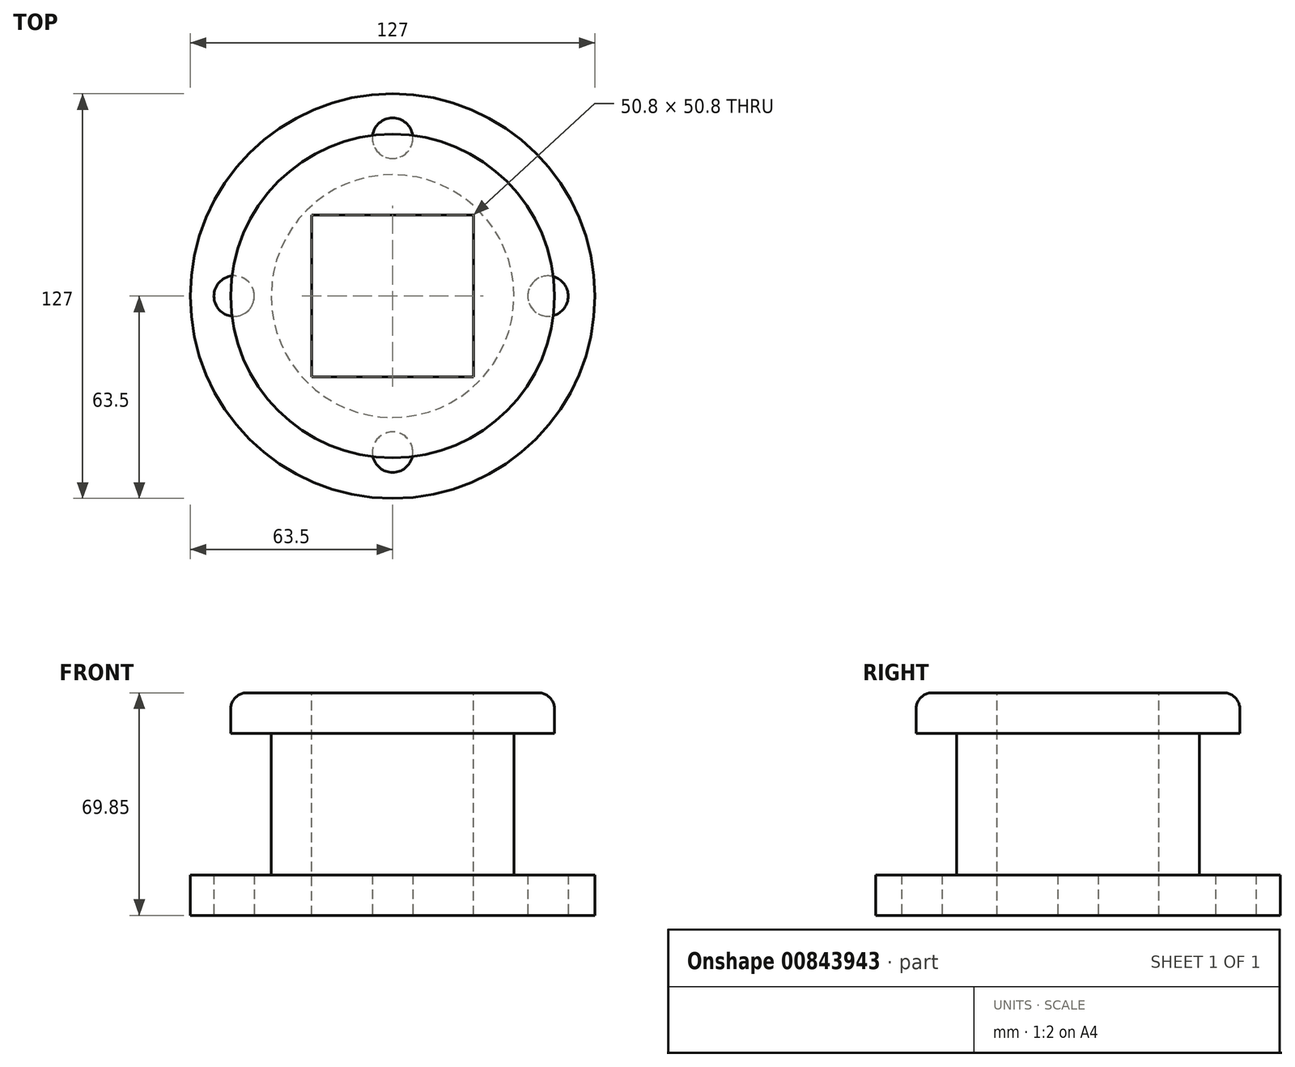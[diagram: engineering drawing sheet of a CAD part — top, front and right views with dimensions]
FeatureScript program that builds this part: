
annotation { "Feature Type Name" : "Feature", "Feature Type Description" : "" }
export const myFeature = defineFeature(function(context is Context, id is Id, definition is map)
    precondition{}
    {
        {
            var Q0;
            Q0=qCreatedBy(makeId("Top.planeOp"),FACE);
            var sketch = newSketch(context, id + "F0", { "sketchPlane" : qUnion([Q0])});
            skCircle(sketch, "E0", {"center": v(0, 0) * mm, "radius": 63.5 * mm});
            skSolve(sketch);
        }
        {
            var Q0;
            Q0 = qSketchRegion(id + "F0", true);
            extrude(context, id + "F1", {"entities" : qUnion([Q0]), "depth" : 12.7 * mm, "offsetDistance" : 25.4 * mm});
        }
        {
            var Q0;
            Q0=qCreatedBy(makeId("Top.planeOp"),FACE);
            var sketch = newSketch(context, id + "F2", { "sketchPlane" : qUnion([Q0])});
            skCircle(sketch, "E1", {"center": v(0, 0) * mm, "radius": 38.1 * mm});
            skSolve(sketch);
        }
        {
            var Q0;
            Q0 = qSketchRegion(id + "F2", true);
            extrude(context, id + "F3", {"entities" : qUnion([Q0]), "operationType" : NewBodyOperationType.ADD, "depth" : 57.15 * mm, "offsetDistance" : 25.4 * mm});
        }
        {
            var Q0;
            Q0=qCreatedBy(makeId("Top.planeOp"),FACE);
            var sketch = newSketch(context, id + "F4", { "sketchPlane" : qUnion([Q0])});
            skCircle(sketch, "E2", {"center": v(-49.74, 0) * mm, "radius": 6.35 * mm});
            skPoint(sketch, "E3.center.orphan", {"position": v(0, 49.55) * mm});
            skPoint(sketch, "E4.center.orphan", {"position": v(48.79, 0) * mm});
            skPoint(sketch, "E5.center.orphan", {"position": v(0, -48.98) * mm});
            skCircle(sketch, "E6", {"center": v(0, 49.55) * mm, "radius": 6.35 * mm});
            skCircle(sketch, "E7", {"center": v(48.79, 0) * mm, "radius": 6.35 * mm});
            skCircle(sketch, "E8", {"center": v(0, -48.98) * mm, "radius": 6.35 * mm});
            skSolve(sketch);
        }
        {
            var Q0;
            Q0 = qSketchRegion(id + "F4", true);
            extrude(context, id + "F5", {"entities" : qUnion([Q0]), "operationType" : NewBodyOperationType.REMOVE, "oppositeDirection" : true, "depth" : 12.7 * mm, "offsetDistance" : 25.4 * mm});
        }
        {
            var Q0;
            Q0 = qSketchRegion(id + "F4", true);
            extrude(context, id + "F6", {"entities" : qUnion([Q0]), "operationType" : NewBodyOperationType.REMOVE, "depth" : 25.4 * mm, "offsetDistance" : 25.4 * mm});
        }
        {
            var Q0;
            Q0 = qSketchRegion(id + "F4", true);
            extrude(context, id + "F7", {"entities" : qUnion([Q0]), "operationType" : NewBodyOperationType.REMOVE, "oppositeDirection" : true, "depth" : 25.4 * mm, "offsetDistance" : 25.4 * mm});
        }
        {
            var Q0;
            Q0=makeQuery(id+"F3.opExtrude","CAP_FACE",FACE,{"disambiguationData":[OSD([sQuery(id+"F2.wireOp",EDGE,"E1")])],"isStart":false});
            var sketch = newSketch(context, id + "F8", { "sketchPlane" : qUnion([Q0])});
            skCircle(sketch, "E9", {"center": v(0, 0) * mm, "radius": 50.8 * mm});
            skSolve(sketch);
        }
        {
            var Q0;
            Q0 = qSketchRegion(id + "F8", true);
            extrude(context, id + "F9", {"entities" : qUnion([Q0]), "operationType" : NewBodyOperationType.ADD, "depth" : 12.7 * mm, "offsetDistance" : 25.4 * mm});
        }
        {
            var Q0;
            Q0=makeQuery(id+"F9.opExtrude","CAP_FACE",FACE,{"disambiguationData":[OSD([sQuery(id+"F8.wireOp",EDGE,"E9")])],"isStart":false});
            var sketch = newSketch(context, id + "F10", { "sketchPlane" : qUnion([Q0])});
            skLineSegment(sketch, "E10.bottom", {"start": v(-25.4, 25.4) * mm, "end": v(25.4, 25.4) * mm});
            skLineSegment(sketch, "E10.top", {"start": v(-25.4, -25.4) * mm, "end": v(25.4, -25.4) * mm});
            skLineSegment(sketch, "E10.left", {"start": v(-25.4, 25.4) * mm, "end": v(-25.4, -25.4) * mm});
            skLineSegment(sketch, "E10.right", {"start": v(25.4, 25.4) * mm, "end": v(25.4, -25.4) * mm});
            skPoint(sketch, "E10.middle", {"position": v(0, 0) * mm});
            skSolve(sketch);
        }
        {
            var Q0;
            Q0 = qSketchRegion(id + "F10", true);
            extrude(context, id + "F11", {"entities" : qUnion([Q0]), "operationType" : NewBodyOperationType.REMOVE, "oppositeDirection" : true, "depth" : 127 * mm, "offsetDistance" : 25.4 * mm});
        }
        {
            var Q0;
            Q0=makeQuery(id+"F9.opExtrude","CAP_EDGE",EDGE,{"disambiguationData":[OSD([sQuery(id+"F8.wireOp",EDGE,"E9")])],"isStart":false});
            fillet(context, id + "F12", {"entities" : qUnion([Q0]), "radius" : 5.08 * mm, "tangentPropagation" : true, "allowEdgeOverflow" : false});
        }
    });
